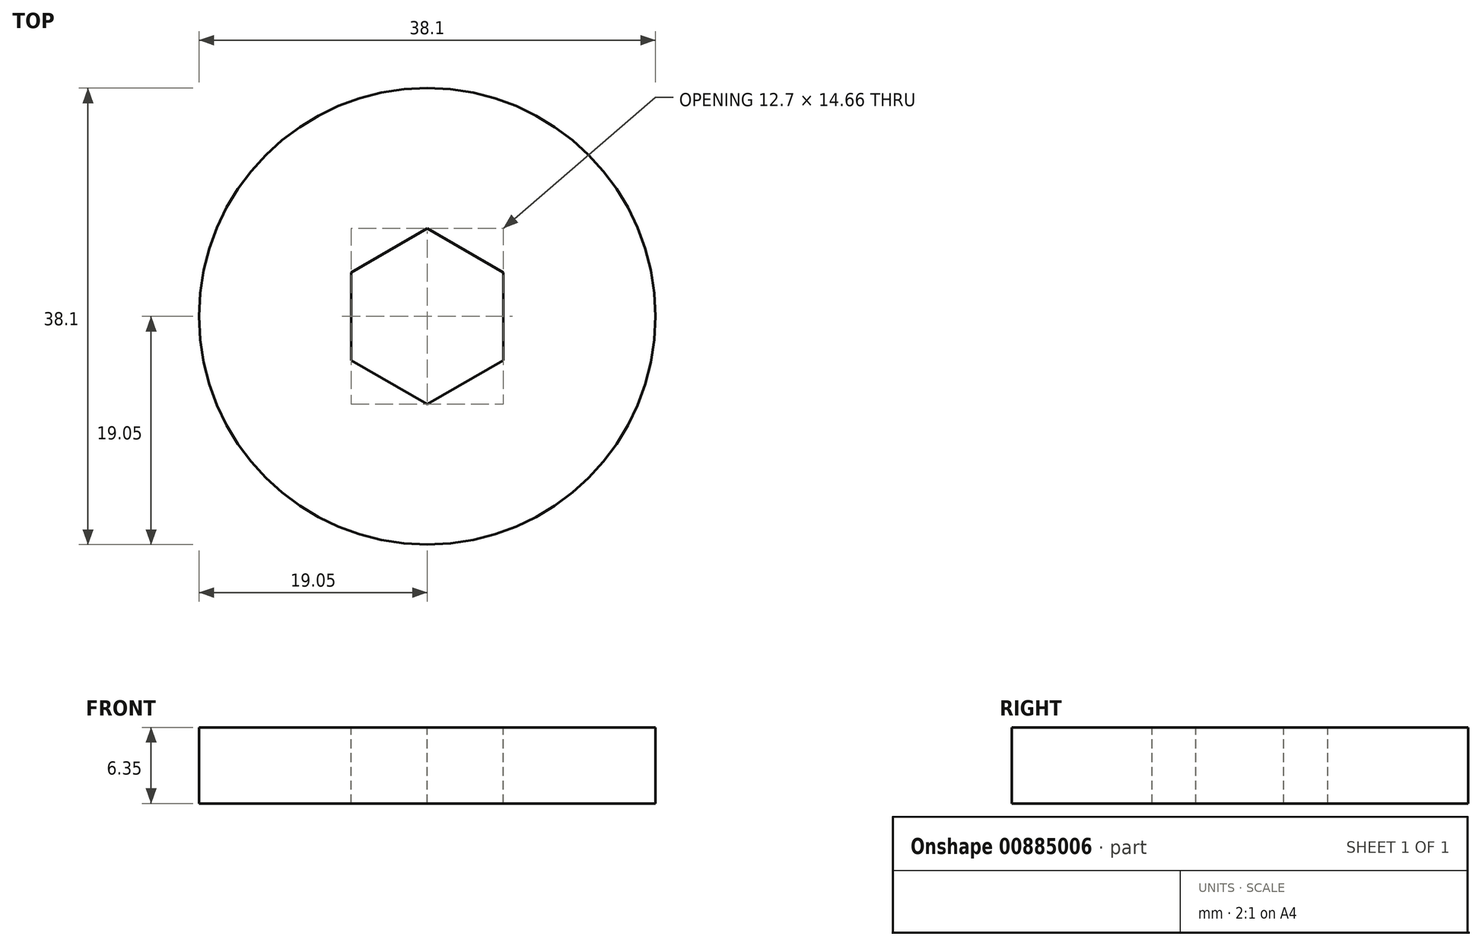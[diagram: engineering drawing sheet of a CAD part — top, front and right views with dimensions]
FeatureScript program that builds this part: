
annotation { "Feature Type Name" : "Feature", "Feature Type Description" : "" }
export const myFeature = defineFeature(function(context is Context, id is Id, definition is map)
    precondition{}
    {
        {
            var Q0;
            Q0=qCreatedBy(makeId("Top.planeOp"),FACE);
            var sketch = newSketch(context, id + "F0", { "sketchPlane" : qUnion([Q0])});
            skCircle(sketch, "E0", {"center": v(0, 0) * mm, "radius": 19.05 * mm});
            skCircle(sketch, "E1.cCircle", {"center": v(0, 0) * mm, "radius": 6.35 * mm, "construction": true});
            skLineSegment(sketch, "E1.0", {"start": v(6.35, 3.67) * mm, "end": v(6.35, -3.67) * mm});
            skLineSegment(sketch, "E1.1", {"start": v(6.35, -3.67) * mm, "end": v(0, -7.33) * mm});
            skLineSegment(sketch, "E1.2", {"start": v(0, -7.33) * mm, "end": v(-6.35, -3.67) * mm});
            skLineSegment(sketch, "E1.3", {"start": v(-6.35, -3.67) * mm, "end": v(-6.35, 3.67) * mm});
            skLineSegment(sketch, "E1.4", {"start": v(-6.35, 3.67) * mm, "end": v(0, 7.33) * mm});
            skLineSegment(sketch, "E1.5", {"start": v(0, 7.33) * mm, "end": v(6.35, 3.67) * mm});
            skPoint(sketch, "E1.0.midPoint", {"position": v(6.35, 0) * mm});
            skSolve(sketch);
        }
        {
            var Q0;
            Q0=makeQuery(id+"F0.imprint","IMPRINT",FACE,{"disambiguationData":[TD([[makeQuery(id+"F0.imprint","IMPRINT",EDGE,{"derivedFrom":sQuery(id+"F0.wireOp",EDGE,"E0")}),1.0]])]});
            extrude(context, id + "F1", {"entities" : qUnion([Q0]), "oppositeDirection" : true, "depth" : 6.35 * mm, "offsetDistance" : 25.4 * mm});
        }
    });
